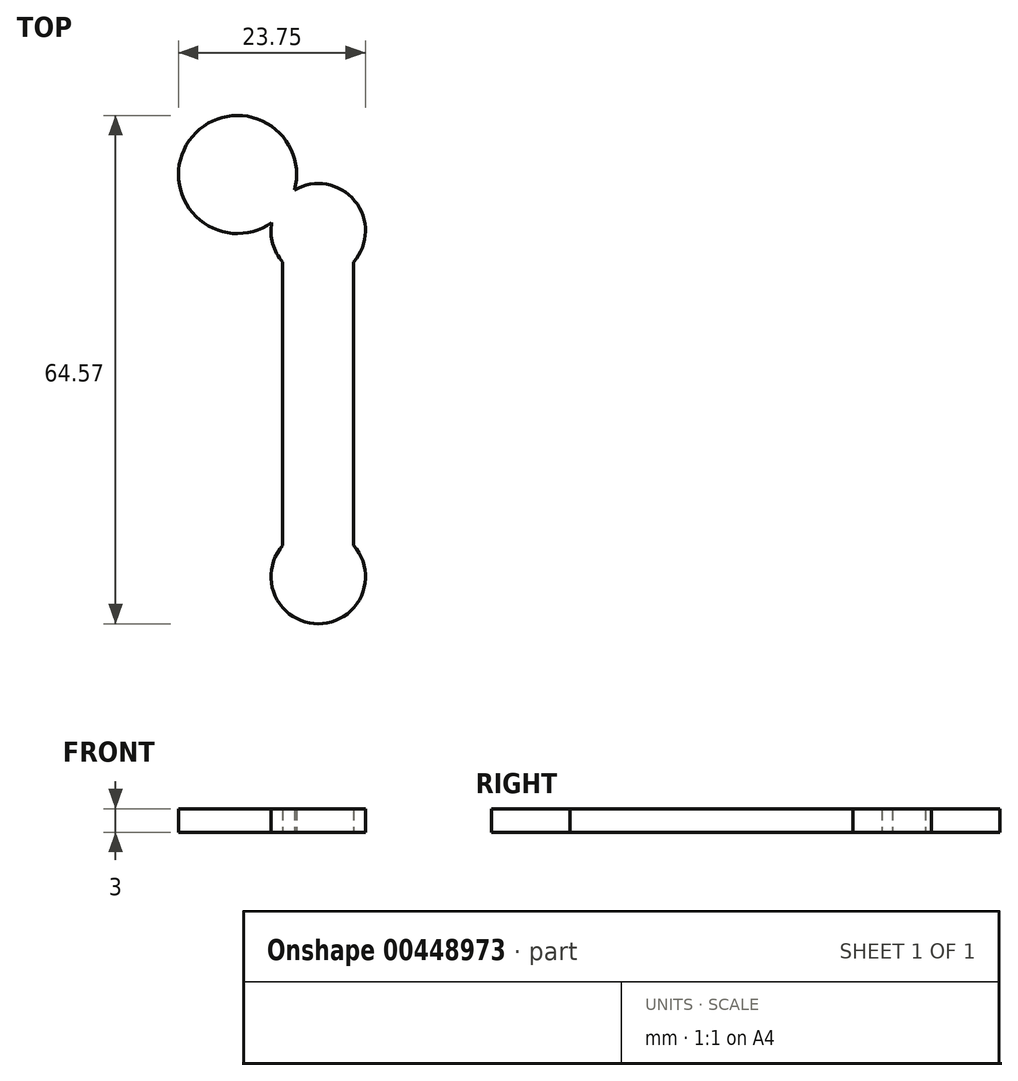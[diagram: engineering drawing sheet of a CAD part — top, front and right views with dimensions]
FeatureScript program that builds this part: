
annotation { "Feature Type Name" : "Feature", "Feature Type Description" : "" }
export const myFeature = defineFeature(function(context is Context, id is Id, definition is map)
    precondition{}
    {
        {
            var Q0;
            Q0=qCreatedBy(makeId("Top.planeOp"),FACE);
            var sketch = newSketch(context, id + "F0", { "sketchPlane" : qUnion([Q0])});
            skLineSegment(sketch, "E0.bottom", {"start": v(-16.52, 22.85) * mm, "end": v(-7.52, 22.85) * mm});
            skLineSegment(sketch, "E0.top", {"start": v(-16.52, -14.15) * mm, "end": v(-7.52, -14.15) * mm});
            skLineSegment(sketch, "E0.left", {"start": v(-16.52, 22.85) * mm, "end": v(-16.52, -14.15) * mm});
            skLineSegment(sketch, "E0.right", {"start": v(-7.52, 22.85) * mm, "end": v(-7.52, -14.15) * mm});
            skCircle(sketch, "E1", {"center": v(-12.02, 25.85) * mm, "radius": 6 * mm});
            skPoint(sketch, "E1.centerSnap0", {"position": v(-12.02, 22.85) * mm});
            skCircle(sketch, "E2", {"center": v(-12.02, -18.07) * mm, "radius": 6 * mm});
            skPoint(sketch, "E2.centerSnap0", {"position": v(-12.02, -14.15) * mm});
            skCircle(sketch, "E3", {"center": v(-22.27, 33) * mm, "radius": 7.5 * mm});
            skSolve(sketch);
        }
        {
            var Q0;
            {var subQ0=sQuery(id+"F0.wireOp",EDGE,"E0.top");Q0=makeQuery(id+"F0.imprint","IMPRINT",FACE,{"disambiguationData":[TD([[makeQuery(id+"F0.imprint","IMPRINT",EDGE,{"derivedFrom":subQ0}),-1.0]])]});}
            var Q1;
            {var subQ0=sQuery(id+"F0.wireOp",EDGE,"E3");var subQ1=sQuery(id+"F0.wireOp",EDGE,"E1");var subQ2=makeQuery(id+"F0.imprint","INTERSECT",VERTEX,{"disambiguationData":[OD(0.0)],"derivedFrom":[subQ1,subQ0]});Q1=makeQuery(id+"F0.imprint","IMPRINT",FACE,{"disambiguationData":[TD([[makeQuery(id+"F0.imprint","IMPRINT",EDGE,{"disambiguationData":[TD([[subQ2,1.0]])],"derivedFrom":subQ1}),-1.0]])]});}
            var Q2;
            {var subQ5=sQuery(id+"F0.wireOp",EDGE,"E0.bottom");Q2=makeQuery(id+"F0.imprint","IMPRINT",FACE,{"disambiguationData":[TD([[makeQuery(id+"F0.imprint","IMPRINT",EDGE,{"derivedFrom":subQ5}),1.0]])]});}
            var Q3;
            {var subQ0=sQuery(id+"F0.wireOp",EDGE,"E0.bottom");Q3=makeQuery(id+"F0.imprint","IMPRINT",FACE,{"disambiguationData":[TD([[makeQuery(id+"F0.imprint","IMPRINT",EDGE,{"derivedFrom":subQ0}),-1.0]])]});}
            var Q4;
            {var subQ0=sQuery(id+"F0.wireOp",EDGE,"E1");var subQ1=sQuery(id+"F0.wireOp",EDGE,"E0.left");var subQ2=makeQuery(id+"F0.imprint","INTERSECT",VERTEX,{"derivedFrom":[subQ1,subQ0]});Q4=makeQuery(id+"F0.imprint","IMPRINT",FACE,{"disambiguationData":[TD([[makeQuery(id+"F0.imprint","IMPRINT",EDGE,{"disambiguationData":[TD([[subQ2,-1.0]])],"derivedFrom":subQ1}),1.0]])]});}
            var Q5;
            {var subQ0=sQuery(id+"F0.wireOp",EDGE,"E0.top");Q5=makeQuery(id+"F0.imprint","IMPRINT",FACE,{"disambiguationData":[TD([[makeQuery(id+"F0.imprint","IMPRINT",EDGE,{"derivedFrom":subQ0}),1.0]])]});}
            var Q6;
            {var subQ0=sQuery(id+"F0.wireOp",EDGE,"E3");var subQ1=sQuery(id+"F0.wireOp",EDGE,"E1");var subQ2=makeQuery(id+"F0.imprint","INTERSECT",VERTEX,{"disambiguationData":[OD(0.0)],"derivedFrom":[subQ1,subQ0]});Q6=makeQuery(id+"F0.imprint","IMPRINT",FACE,{"disambiguationData":[TD([[makeQuery(id+"F0.imprint","IMPRINT",EDGE,{"disambiguationData":[TD([[subQ2,1.0]])],"derivedFrom":subQ1}),1.0]])]});}
            extrude(context, id + "F1", {"entities" : qUnion([Q0, Q1, Q2, Q3, Q4, Q5, Q6]), "depth" : 3 * mm});
        }
    });
